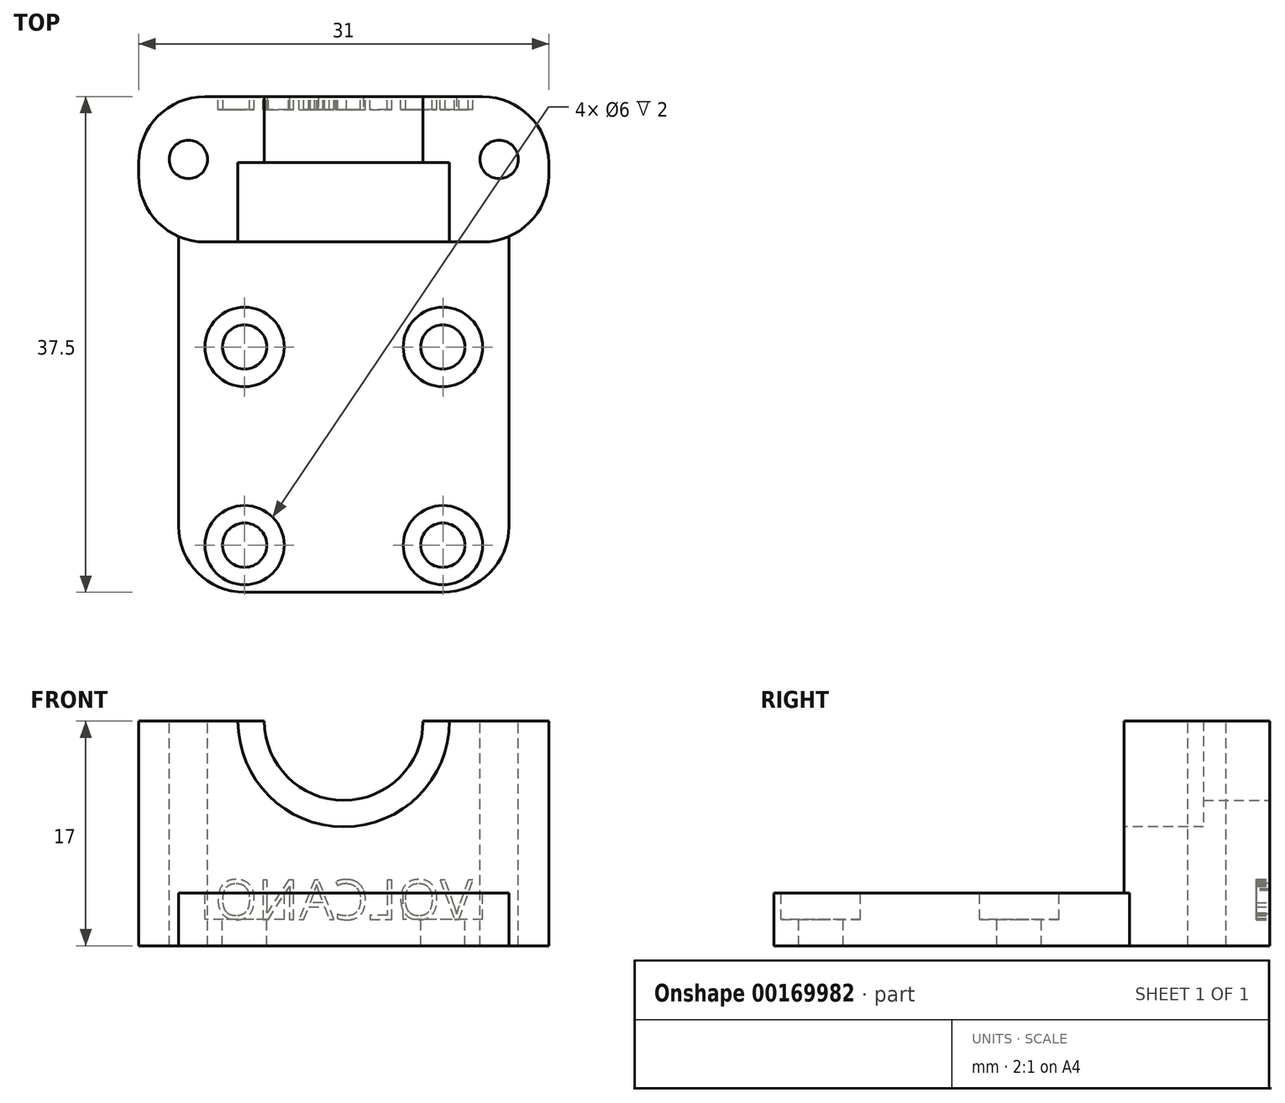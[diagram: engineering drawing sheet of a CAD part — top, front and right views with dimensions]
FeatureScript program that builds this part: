
annotation { "Feature Type Name" : "Feature", "Feature Type Description" : "" }
export const myFeature = defineFeature(function(context is Context, id is Id, definition is map)
    precondition{}
    {
        {
            var Q0;
            Q0=qCreatedBy(makeId("Top.planeOp"),FACE);
            var sketch = newSketch(context, id + "F0", { "sketchPlane" : qUnion([Q0])});
            skLineSegment(sketch, "E0.bottom", {"start": v(0, 0) * mm, "end": v(25, 0) * mm});
            skLineSegment(sketch, "E0.top", {"start": v(0, 30) * mm, "end": v(25, 30) * mm});
            skLineSegment(sketch, "E0.left", {"start": v(0, 0) * mm, "end": v(0, 30) * mm});
            skLineSegment(sketch, "E0.right", {"start": v(25, 0) * mm, "end": v(25, 30) * mm});
            skLineSegment(sketch, "E1.top", {"start": v(0, 37.5) * mm, "end": v(25, 37.5) * mm});
            skLineSegment(sketch, "E1.left", {"start": v(0, 30) * mm, "end": v(0, 37.5) * mm});
            skLineSegment(sketch, "E1.right", {"start": v(25, 30) * mm, "end": v(25, 37.5) * mm});
            skSolve(sketch);
        }
        {
            var Q0;
            Q0=qSketchRegion(id+"F0",true);
            extrude(context, id + "F1", {"entities" : qUnion([Q0]), "depth" : 4 * mm});
        }
        {
            var Q0;
            Q0=makeQuery(id+"F1.opExtrude","CAP_FACE",FACE,{"disambiguationData":[OSD([sQuery(id+"F0.wireOp",EDGE,"E0.bottom"),sQuery(id+"F0.wireOp",EDGE,"E0.top"),sQuery(id+"F0.wireOp",EDGE,"E0.left"),sQuery(id+"F0.wireOp",EDGE,"E0.right")])],"isStart":false});
            var sketch = newSketch(context, id + "F2", { "sketchPlane" : qUnion([Q0])});
            skCircle(sketch, "E2", {"center": v(5, 18.56) * mm, "radius": 1.68 * mm});
            skCircle(sketch, "E3", {"center": v(20, 18.56) * mm, "radius": 1.68 * mm});
            skCircle(sketch, "E4", {"center": v(5, 3.56) * mm, "radius": 1.68 * mm});
            skCircle(sketch, "E5", {"center": v(20, 3.56) * mm, "radius": 1.68 * mm});
            skLineSegment(sketch, "E6", {"start": v(5, 18.56) * mm, "end": v(0, 18.56) * mm});
            skLineSegment(sketch, "E7", {"start": v(20, 3.56) * mm, "end": v(25, 3.56) * mm});
            skCircle(sketch, "E8", {"center": v(5, 18.56) * mm, "radius": 3 * mm});
            skCircle(sketch, "E9", {"center": v(20, 18.56) * mm, "radius": 3 * mm});
            skCircle(sketch, "E10", {"center": v(5, 3.56) * mm, "radius": 3 * mm});
            skCircle(sketch, "E11", {"center": v(20, 3.56) * mm, "radius": 3 * mm});
            skSolve(sketch);
        }
        {
            var Q0;
            Q0=makeQuery(id+"F2.imprint","IMPRINT",FACE,{"disambiguationData":[TD([[makeQuery(id+"F2.imprint","IMPRINT",EDGE,{"derivedFrom":sQuery(id+"F2.wireOp",EDGE,"E2")}),1.0]])]});
            var Q1;
            Q1=makeQuery(id+"F2.imprint","IMPRINT",FACE,{"disambiguationData":[TD([[makeQuery(id+"F2.imprint","IMPRINT",EDGE,{"derivedFrom":sQuery(id+"F2.wireOp",EDGE,"E3")}),1.0]])]});
            var Q2;
            Q2=makeQuery(id+"F2.imprint","IMPRINT",FACE,{"disambiguationData":[TD([[makeQuery(id+"F2.imprint","IMPRINT",EDGE,{"derivedFrom":sQuery(id+"F2.wireOp",EDGE,"E5")}),1.0]])]});
            var Q3;
            Q3=makeQuery(id+"F2.imprint","IMPRINT",FACE,{"disambiguationData":[TD([[makeQuery(id+"F2.imprint","IMPRINT",EDGE,{"derivedFrom":sQuery(id+"F2.wireOp",EDGE,"E4")}),1.0]])]});
            extrude(context, id + "F3", {"entities" : qUnion([Q0, Q1, Q2, Q3]), "operationType" : NewBodyOperationType.REMOVE, "oppositeDirection" : true, "depth" : 25 * mm});
        }
        {
            var Q0;
            Q0=makeQuery(id+"F1.opExtrude","CAP_FACE",FACE,{"disambiguationData":[OSD([sQuery(id+"F0.wireOp",EDGE,"E0.bottom"),sQuery(id+"F0.wireOp",EDGE,"E0.top"),sQuery(id+"F0.wireOp",EDGE,"E0.left"),sQuery(id+"F0.wireOp",EDGE,"E0.right")])],"isStart":false});
            var sketch = newSketch(context, id + "F4", { "sketchPlane" : qUnion([Q0])});
            skLineSegment(sketch, "E12.bottom", {"start": v(0, 37.5) * mm, "end": v(25, 37.5) * mm});
            skLineSegment(sketch, "E12.top", {"start": v(0, 26.5) * mm, "end": v(25, 26.5) * mm});
            skLineSegment(sketch, "E12.left", {"start": v(0, 37.5) * mm, "end": v(0, 26.5) * mm});
            skLineSegment(sketch, "E12.right", {"start": v(25, 37.5) * mm, "end": v(25, 26.5) * mm});
            skSolve(sketch);
        }
        {
            var Q0;
            Q0=qSketchRegion(id+"F4",true);
            extrude(context, id + "F5", {"entities" : qUnion([Q0]), "operationType" : NewBodyOperationType.ADD, "depth" : 13 * mm});
        }
        {
            var Q0;
            Q0=makeQuery(id+"F5.boolean.opBoolean","MERGE",FACE,{"derivedFrom":[makeQuery(id+"F1.opExtrude","SWEPT_FACE",FACE,{"disambiguationData":[OSD([sQuery(id+"F0.wireOp",EDGE,"E1.top")])]}),makeQuery(id+"F5.opExtrude","SWEPT_FACE",FACE,{"disambiguationData":[OSD([sQuery(id+"F4.wireOp",EDGE,"E12.bottom")])]})]});
            var sketch = newSketch(context, id + "F6", { "sketchPlane" : qUnion([Q0])});
            skCircle(sketch, "E13", {"center": v(-12.5, 17) * mm, "radius": 6 * mm});
            skSolve(sketch);
        }
        {
            var Q0;
            {var subQ0=makeQuery(id+"F5.opExtrude","CAP_EDGE",EDGE,{"disambiguationData":[OSD([sQuery(id+"F4.wireOp",EDGE,"3fca9e3f-73a0-4211-9b6f-f3487c54c975.bottom")])],"isStart":false});var subQ1=sQuery(id+"F6.wireOp",EDGE,"E13");var subQ3=makeQuery(id+"F6.imprint","INTERSECT",VERTEX,{"disambiguationData":[OD(0.0)],"derivedFrom":[subQ0,subQ1]});Q0=makeQuery(id+"F6.imprint","IMPRINT",FACE,{"disambiguationData":[TD([[makeQuery(id+"F6.imprint","IMPRINT",EDGE,{"disambiguationData":[TD([[subQ3,1.0]])],"derivedFrom":subQ1}),1.0]])]});}
            var Q1;
            {var subQ0=sQuery(id+"F6.wireOp",EDGE,"E13");var subQ1=makeQuery(id+"F5.opExtrude","CAP_EDGE",EDGE,{"disambiguationData":[OSD([sQuery(id+"F4.wireOp",EDGE,"E12.top")])],"isStart":false});var subQ2=makeQuery(id+"F6.imprint","INTERSECT",VERTEX,{"disambiguationData":[OD(0.0)],"derivedFrom":[subQ1,subQ0]});Q1=makeQuery(id+"F6.imprint","IMPRINT",FACE,{"disambiguationData":[TD([[makeQuery(id+"F6.imprint","IMPRINT",EDGE,{"disambiguationData":[TD([[subQ2,-1.0]])],"derivedFrom":subQ0}),1.0]])]});}
            extrude(context, id + "F7", {"entities" : qUnion([Q0, Q1]), "operationType" : NewBodyOperationType.REMOVE, "oppositeDirection" : true, "depth" : 6 * mm});
        }
        {
            var Q0;
            Q0=makeQuery(id+"F5.opExtrude","SWEPT_FACE",FACE,{"disambiguationData":[OSD([sQuery(id+"F4.wireOp",EDGE,"E12.top")])]});
            var sketch = newSketch(context, id + "F8", { "sketchPlane" : qUnion([Q0])});
            skCircle(sketch, "E14", {"center": v(12.5, 17) * mm, "radius": 8 * mm});
            skSolve(sketch);
        }
        {
            var Q0;
            Q0=qSketchRegion(id+"F8",true);
            extrude(context, id + "F9", {"entities" : qUnion([Q0]), "operationType" : NewBodyOperationType.REMOVE, "oppositeDirection" : true, "depth" : 6 * mm});
        }
        {
            var Q0;
            Q0=makeQuery(id+"F2.imprint","IMPRINT",FACE,{"disambiguationData":[TD([[makeQuery(id+"F2.imprint","IMPRINT",EDGE,{"derivedFrom":sQuery(id+"F2.wireOp",EDGE,"E2")}),-1.0]])]});
            var Q1;
            Q1=makeQuery(id+"F2.imprint","IMPRINT",FACE,{"disambiguationData":[TD([[makeQuery(id+"F2.imprint","IMPRINT",EDGE,{"derivedFrom":sQuery(id+"F2.wireOp",EDGE,"E3")}),-1.0]])]});
            var Q2;
            Q2=makeQuery(id+"F2.imprint","IMPRINT",FACE,{"disambiguationData":[TD([[makeQuery(id+"F2.imprint","IMPRINT",EDGE,{"derivedFrom":sQuery(id+"F2.wireOp",EDGE,"E5")}),-1.0]])]});
            var Q3;
            Q3=makeQuery(id+"F2.imprint","IMPRINT",FACE,{"disambiguationData":[TD([[makeQuery(id+"F2.imprint","IMPRINT",EDGE,{"derivedFrom":sQuery(id+"F2.wireOp",EDGE,"E4")}),-1.0]])]});
            extrude(context, id + "F10", {"entities" : qUnion([Q0, Q1, Q2, Q3]), "operationType" : NewBodyOperationType.REMOVE, "oppositeDirection" : true, "depth" : 2 * mm});
        }
        {
            var Q0;
            Q0=makeQuery(id+"F5.boolean.opBoolean","MERGE",FACE,{"derivedFrom":[makeQuery(id+"F1.opExtrude","SWEPT_FACE",FACE,{"disambiguationData":[OSD([sQuery(id+"F0.wireOp",EDGE,"E0.left")])]}),makeQuery(id+"F5.opExtrude","SWEPT_FACE",FACE,{"disambiguationData":[OSD([sQuery(id+"F4.wireOp",EDGE,"3fca9e3f-73a0-4211-9b6f-f3487c54c975.left")])]})]});
            var sketch = newSketch(context, id + "F11", { "sketchPlane" : qUnion([Q0])});
            skLineSegment(sketch, "E15.bottom", {"start": v(-37.5, 0) * mm, "end": v(-26.5, 0) * mm});
            skLineSegment(sketch, "E15.top", {"start": v(-37.5, 17) * mm, "end": v(-26.5, 17) * mm});
            skLineSegment(sketch, "E15.left", {"start": v(-37.5, 0) * mm, "end": v(-37.5, 17) * mm});
            skLineSegment(sketch, "E15.right", {"start": v(-26.5, 0) * mm, "end": v(-26.5, 17) * mm});
            skSolve(sketch);
        }
        {
            var Q0;
            Q0=qSketchRegion(id+"F11",true);
            extrude(context, id + "F12", {"entities" : qUnion([Q0]), "operationType" : NewBodyOperationType.ADD, "depth" : 3 * mm});
        }
        {
            var Q0;
            Q0=makeQuery(id+"F5.boolean.opBoolean","MERGE",FACE,{"derivedFrom":[makeQuery(id+"F1.opExtrude","SWEPT_FACE",FACE,{"disambiguationData":[OSD([sQuery(id+"F0.wireOp",EDGE,"E0.right")])]}),makeQuery(id+"F5.opExtrude","SWEPT_FACE",FACE,{"disambiguationData":[OSD([sQuery(id+"F4.wireOp",EDGE,"3fca9e3f-73a0-4211-9b6f-f3487c54c975.right")])]})]});
            var sketch = newSketch(context, id + "F13", { "sketchPlane" : qUnion([Q0])});
            skLineSegment(sketch, "E16.bottom", {"start": v(37.5, 17) * mm, "end": v(26.5, 17) * mm});
            skLineSegment(sketch, "E16.top", {"start": v(37.5, 0) * mm, "end": v(26.5, 0) * mm});
            skLineSegment(sketch, "E16.left", {"start": v(37.5, 17) * mm, "end": v(37.5, 0) * mm});
            skLineSegment(sketch, "E16.right", {"start": v(26.5, 17) * mm, "end": v(26.5, 0) * mm});
            skSolve(sketch);
        }
        {
            var Q0;
            Q0=qSketchRegion(id+"F13",true);
            extrude(context, id + "F14", {"entities" : qUnion([Q0]), "operationType" : NewBodyOperationType.ADD, "depth" : 3 * mm});
        }
        {
            var Q0;
            {var subQ0=sQuery(id+"F4.wireOp",EDGE,"E12.bottom");var subQ1=sQuery(id+"F4.wireOp",EDGE,"E12.top");var subQ3=sQuery(id+"F4.wireOp",EDGE,"E12.right");Q0=makeQuery(id+"F14.boolean.opBoolean","MERGE",FACE,{"derivedFrom":[makeQuery(id+"F9.boolean.opBoolean","SPLIT",FACE,{"disambiguationData":[TD([makeQuery(id+"F5.opExtrude","SWEPT_FACE",FACE,{"disambiguationData":[OSD([subQ3])]})])],"derivedFrom":makeQuery(id+"F5.opExtrude","CAP_FACE",FACE,{"disambiguationData":[OSD([subQ0,subQ1,sQuery(id+"F4.wireOp",EDGE,"E12.left"),subQ3])],"isStart":false})}),makeQuery(id+"F14.opExtrude","SWEPT_FACE",FACE,{"disambiguationData":[OSD([sQuery(id+"F13.wireOp",EDGE,"E16.bottom")])]})]});}
            var sketch = newSketch(context, id + "F15", { "sketchPlane" : qUnion([Q0])});
            skCircle(sketch, "E17", {"center": v(0.75, 32.75) * mm, "radius": 1.45 * mm});
            skCircle(sketch, "E18", {"center": v(24.25, 32.75) * mm, "radius": 1.45 * mm});
            skSolve(sketch);
        }
        {
            var Q0;
            Q0=qSketchRegion(id+"F15",true);
            extrude(context, id + "F16", {"entities" : qUnion([Q0]), "operationType" : NewBodyOperationType.REMOVE, "oppositeDirection" : true, "depth" : 25 * mm});
        }
        {
            var Q0;
            Q0=makeQuery(id+"F12.opExtrude","CAP_EDGE",EDGE,{"disambiguationData":[OSD([sQuery(id+"F11.wireOp",EDGE,"E15.left")])],"isStart":false});
            var Q1;
            Q1=makeQuery(id+"F12.opExtrude","CAP_EDGE",EDGE,{"disambiguationData":[OSD([sQuery(id+"F11.wireOp",EDGE,"E15.right")])],"isStart":false});
            var Q2;
            Q2=makeQuery(id+"F14.opExtrude","CAP_EDGE",EDGE,{"disambiguationData":[OSD([sQuery(id+"F13.wireOp",EDGE,"E16.right")])],"isStart":false});
            var Q3;
            Q3=makeQuery(id+"F14.opExtrude","CAP_EDGE",EDGE,{"disambiguationData":[OSD([sQuery(id+"F13.wireOp",EDGE,"E16.left")])],"isStart":false});
            var Q4;
            Q4=makeQuery(id+"F1.opExtrude","SWEPT_EDGE",EDGE,{"disambiguationData":[OSD([sQuery(id+"F0.wireOp",EDGE,"E0.bottom"),sQuery(id+"F0.wireOp",EDGE,"E0.right")])]});
            var Q5;
            Q5=makeQuery(id+"F1.opExtrude","SWEPT_EDGE",EDGE,{"disambiguationData":[OSD([sQuery(id+"F0.wireOp",EDGE,"E0.bottom"),sQuery(id+"F0.wireOp",EDGE,"E0.left")])]});
            fillet(context, id + "F17", {"entities" : qUnion([Q0, Q1, Q2, Q3, Q4, Q5]), "radius" : 5 * mm, "tangentPropagation" : true, "allowEdgeOverflow" : false});
        }
        {
            var Q0;
            Q0=makeQuery(id+"F2.imprint","IMPRINT",FACE,{"disambiguationData":[TD([[makeQuery(id+"F2.imprint","IMPRINT",EDGE,{"derivedFrom":sQuery(id+"F2.wireOp",EDGE,"E2")}),-1.0]])]});
            var Q1;
            Q1=makeQuery(id+"F2.imprint","IMPRINT",FACE,{"disambiguationData":[TD([[makeQuery(id+"F2.imprint","IMPRINT",EDGE,{"derivedFrom":sQuery(id+"F2.wireOp",EDGE,"E3")}),-1.0]])]});
            var Q2;
            Q2=makeQuery(id+"F2.imprint","IMPRINT",FACE,{"disambiguationData":[TD([[makeQuery(id+"F2.imprint","IMPRINT",EDGE,{"derivedFrom":sQuery(id+"F2.wireOp",EDGE,"E2")}),1.0]])]});
            var Q3;
            Q3=makeQuery(id+"F2.imprint","IMPRINT",FACE,{"disambiguationData":[TD([[makeQuery(id+"F2.imprint","IMPRINT",EDGE,{"derivedFrom":sQuery(id+"F2.wireOp",EDGE,"E3")}),1.0]])]});
            extrude(context, id + "F18", {"entities" : qUnion([Q0, Q1, Q2, Q3]), "operationType" : NewBodyOperationType.REMOVE, "depth" : 25 * mm});
        }
        {
            var Q0;
            Q0=makeQuery(id+"F14.boolean.opBoolean","MERGE",FACE,{"derivedFrom":[makeQuery(id+"F12.boolean.opBoolean","MERGE",FACE,{"derivedFrom":[makeQuery(id+"F5.boolean.opBoolean","MERGE",FACE,{"derivedFrom":[makeQuery(id+"F1.opExtrude","SWEPT_FACE",FACE,{"disambiguationData":[OSD([sQuery(id+"F0.wireOp",EDGE,"E1.top")])]}),makeQuery(id+"F5.opExtrude","SWEPT_FACE",FACE,{"disambiguationData":[OSD([sQuery(id+"F4.wireOp",EDGE,"E12.bottom")])]})]}),makeQuery(id+"F12.opExtrude","SWEPT_FACE",FACE,{"disambiguationData":[OSD([sQuery(id+"F11.wireOp",EDGE,"E15.left")])]})]}),makeQuery(id+"F14.opExtrude","SWEPT_FACE",FACE,{"disambiguationData":[OSD([sQuery(id+"F13.wireOp",EDGE,"E16.left")])]})]});
            var sketch = newSketch(context, id + "F19", { "sketchPlane" : qUnion([Q0])});
            skText(sketch, "E19", { "text": "VOLCANO", "fontName": "OpenSans-Regular.ttf"});
            const initialGuessF19  = {"E19": [-0.02228, 0.002, 1, 0, 0.003]};
            skSetInitialGuess(sketch, initialGuessF19);
            skSolve(sketch);
        }
        {
            var Q0;
            Q0 = qSketchRegion(id + "F19", true);
            extrude(context, id + "F20", {"entities" : qUnion([Q0]), "operationType" : NewBodyOperationType.REMOVE, "oppositeDirection" : true, "depth" : 1 * mm});
        }
    });
